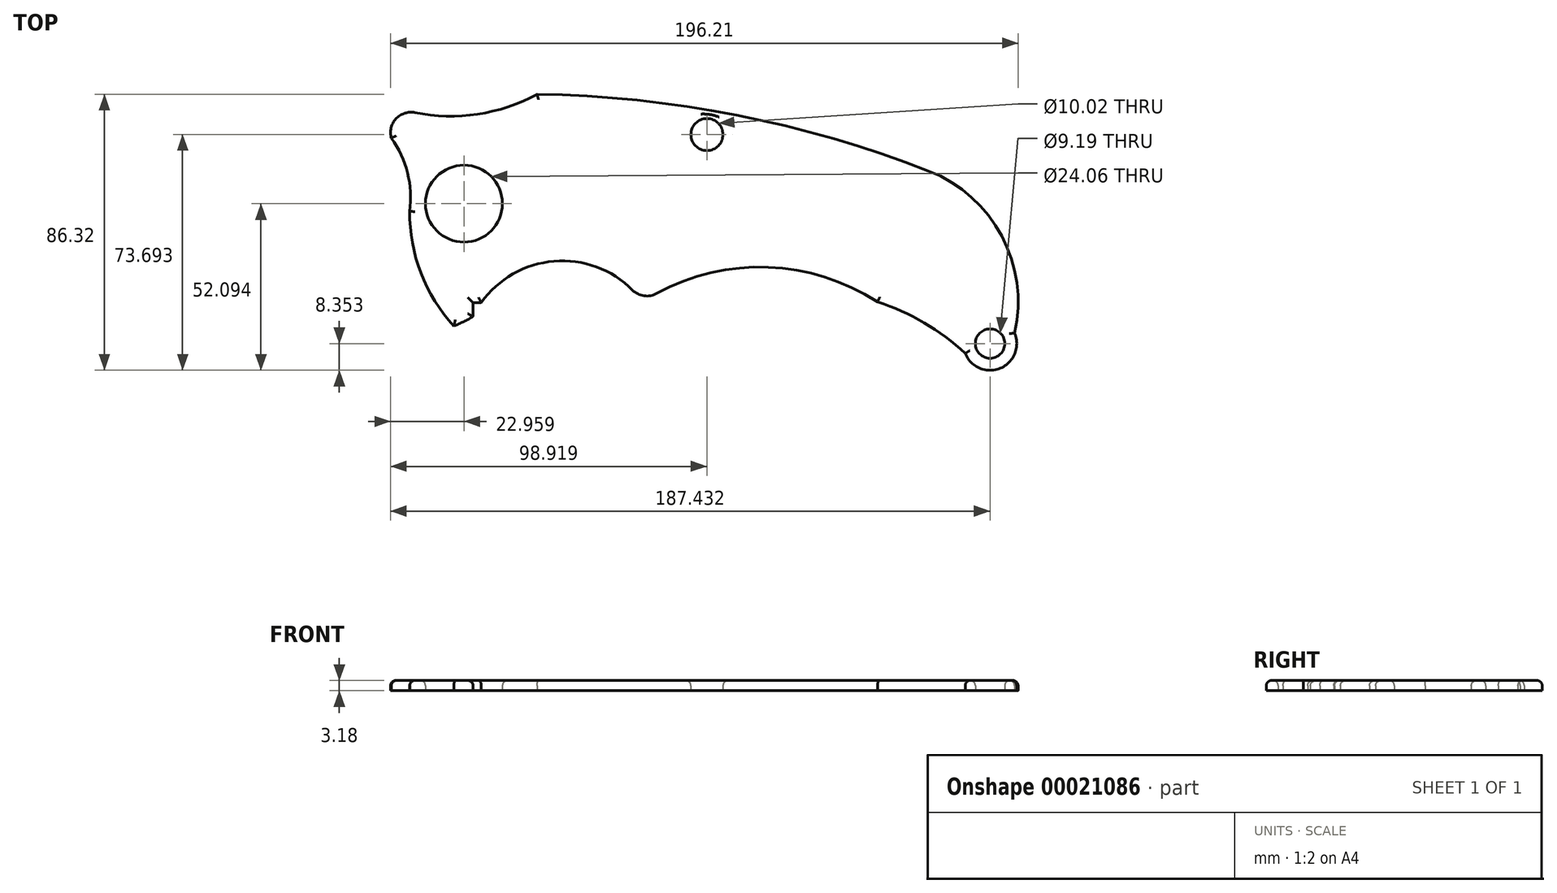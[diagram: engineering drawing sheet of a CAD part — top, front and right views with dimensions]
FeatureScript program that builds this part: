
annotation { "Feature Type Name" : "Feature", "Feature Type Description" : "" }
export const myFeature = defineFeature(function(context is Context, id is Id, definition is map)
    precondition{}
    {
        {
            var Q0;
            Q0=qCreatedBy(makeId("Top.planeOp"),FACE);
            var sketch = newSketch(context, id + "F0", { "sketchPlane" : qUnion([Q0])});
            skPoint(sketch, "E0", {"position": v(70.46, 29.17) * mm});
            skPoint(sketch, "E1", {"position": v(-183.45, 100.22) * mm});
            skCircle(sketch, "E2", {"center": v(150.83, -40.4) * mm, "radius": 4.6 * mm});
            skCircle(sketch, "E3", {"center": v(62.32, 24.94) * mm, "radius": 5 * mm});
            skPoint(sketch, "E4.visualSharp", {"position": v(163.12, 0) * mm});
            skArc(sketch, "E4.filletArc", {"start": v(143.08, -43.5) * mm, "mid": v(154.02, -48.11) * mm, "end": v(158.51, -37.13) * mm});
            skPoint(sketch, "E5.visualSharp", {"position": v(133.35, -13.7) * mm});
            skPoint(sketch, "E6.visualSharp", {"position": v(0, 41.71) * mm});
            skPoint(sketch, "E7", {"position": v(101.44, -41.08) * mm});
            skArc(sketch, "E8", {"start": v(39.03, -23.66) * mm, "mid": v(14.48, -14.65) * mm, "end": v(-8.22, -27.65) * mm});
            skArc(sketch, "E9", {"start": v(115.64, -27.38) * mm, "mid": v(81.47, -16.53) * mm, "end": v(46.58, -24.75) * mm});
            skArc(sketch, "E10", {"start": v(143.08, -43.5) * mm, "mid": v(130.25, -33.93) * mm, "end": v(115.64, -27.38) * mm});
            skArc(sketch, "E11", {"start": v(-28.99, 31.8) * mm, "mid": v(-9.37, 31.31) * mm, "end": v(9.24, 37.57) * mm});
            skArc(sketch, "E12", {"start": v(131.62, 13.59) * mm, "mid": v(71.5, 31.05) * mm, "end": v(9.24, 37.57) * mm});
            skArc(sketch, "E13", {"start": v(131.62, 13.59) * mm, "mid": v(154.48, -6.78) * mm, "end": v(158.51, -37.13) * mm});
            skLineSegment(sketch, "E14", {"start": v(-10.78, -31.98) * mm, "end": v(-10.78, -17.92) * mm});
            skArc(sketch, "E15", {"start": v(-5.68, -8.23) * mm, "mid": v(-2.35, -5) * mm, "end": v(-0.25, -0.88) * mm});
            skArc(sketch, "E16", {"start": v(116.6, 0) * mm, "mid": v(63.7, 6.82) * mm, "end": v(10.38, 7.33) * mm});
            skPoint(sketch, "E17.visualSharp", {"position": v(42.2, -27.38) * mm});
            skArc(sketch, "E17.filletArc", {"start": v(39.03, -23.66) * mm, "mid": v(42.63, -25.47) * mm, "end": v(46.58, -24.75) * mm});
            skPoint(sketch, "E18.visualSharp", {"position": v(-43.1, 36.68) * mm});
            skArc(sketch, "E18.filletArc", {"start": v(-28.99, 31.8) * mm, "mid": v(-34.92, 29.89) * mm, "end": v(-36.35, 23.82) * mm});
            skPoint(sketch, "E19.visualSharp", {"position": v(-10.78, -10.4) * mm});
            skArc(sketch, "E19.filletArc", {"start": v(-5.68, -8.23) * mm, "mid": v(-9.43, -12.44) * mm, "end": v(-10.78, -17.92) * mm});
            skPoint(sketch, "E20.visualSharp", {"position": v(0, 6.69) * mm});
            skArc(sketch, "E20.filletArc", {"start": v(10.38, 7.33) * mm, "mid": v(3.78, 4.9) * mm, "end": v(-0.25, -0.88) * mm});
            skArc(sketch, "E21", {"start": v(-30.63, 0.96) * mm, "mid": v(-27.1, -18.3) * mm, "end": v(-16.78, -34.95) * mm});
            skArc(sketch, "E22", {"start": v(-16.78, -34.95) * mm, "mid": v(-13.74, -33.54) * mm, "end": v(-10.78, -31.98) * mm});
            skLineSegment(sketch, "E23", {"start": v(-8.22, -27.65) * mm, "end": v(-10.78, -27.65) * mm});
            skArc(sketch, "E24", {"start": v(-30.63, 0.96) * mm, "mid": v(-31.27, 12.94) * mm, "end": v(-36.35, 23.82) * mm});
            skCircle(sketch, "E25", {"center": v(-13.64, 3.34) * mm, "radius": 12.03 * mm});
            skSolve(sketch);
        }
        {
            var Q0;
            Q0=makeQuery(id+"F0.imprint","IMPRINT",FACE,{"disambiguationData":[TD([[makeQuery(id+"F0.imprint","IMPRINT",EDGE,{"derivedFrom":sQuery(id+"F0.wireOp",EDGE,"E2")}),-1.0]])]});
            extrude(context, id + "F1", {"entities" : qUnion([Q0]), "depth" : 3.17 * mm});
        }
        {
            var Q0;
            Q0=makeQuery(id+"F1.opExtrude","CAP_FACE",FACE,{"disambiguationData":[OSD([sQuery(id+"F0.wireOp",EDGE,"E2"),sQuery(id+"F0.wireOp",EDGE,"E3"),sQuery(id+"F0.wireOp",EDGE,"E4.filletArc"),sQuery(id+"F0.wireOp",EDGE,"E8"),sQuery(id+"F0.wireOp",EDGE,"E9"),sQuery(id+"F0.wireOp",EDGE,"E10"),sQuery(id+"F0.wireOp",EDGE,"E11"),sQuery(id+"F0.wireOp",EDGE,"E12"),sQuery(id+"F0.wireOp",EDGE,"E13"),sQuery(id+"F0.wireOp",EDGE,"E14"),sQuery(id+"F0.wireOp",EDGE,"E17.filletArc"),sQuery(id+"F0.wireOp",EDGE,"E18.filletArc"),sQuery(id+"F0.wireOp",EDGE,"E21"),sQuery(id+"F0.wireOp",EDGE,"E22"),sQuery(id+"F0.wireOp",EDGE,"E23"),sQuery(id+"F0.wireOp",EDGE,"E24"),sQuery(id+"F0.wireOp",EDGE,"E25")])],"isStart":false});
            fillet(context, id + "F2", {"entities" : qUnion([Q0]), "radius" : 1.65 * mm, "tangentPropagation" : true, "allowEdgeOverflow" : false});
        }
    });
